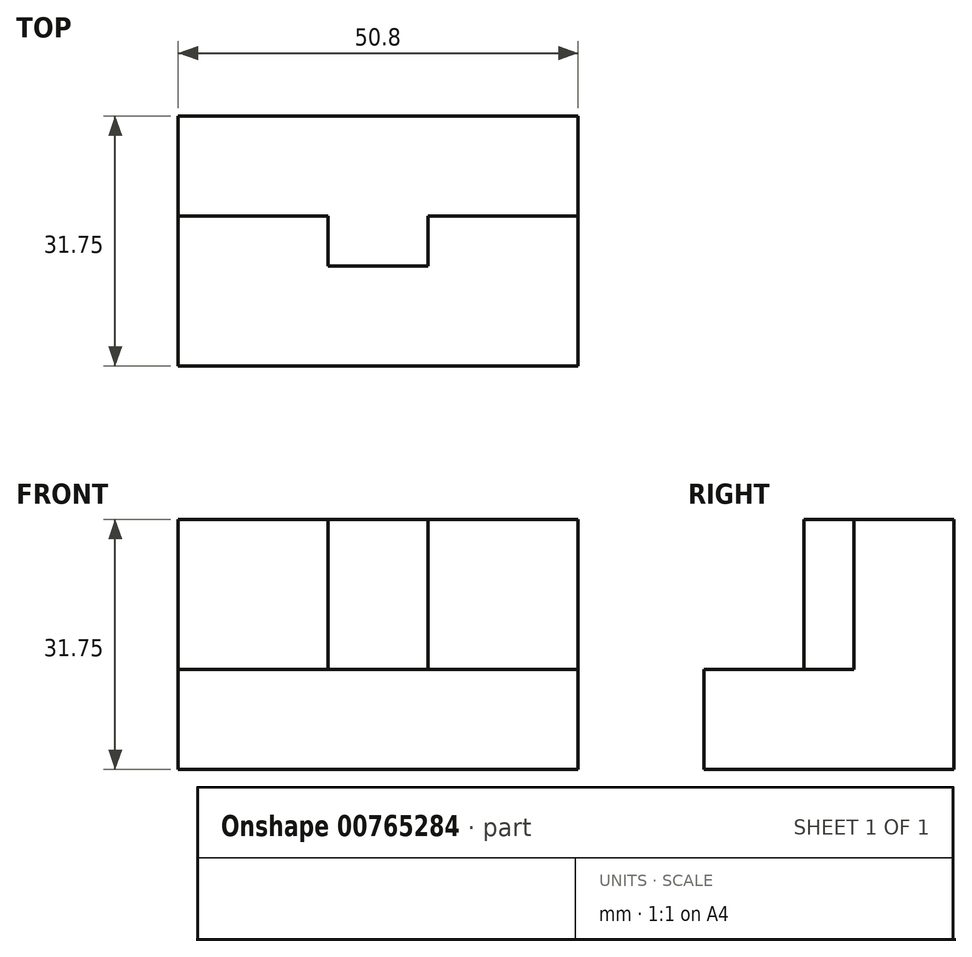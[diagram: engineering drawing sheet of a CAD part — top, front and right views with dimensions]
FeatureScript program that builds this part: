
annotation { "Feature Type Name" : "Feature", "Feature Type Description" : "" }
export const myFeature = defineFeature(function(context is Context, id is Id, definition is map)
    precondition{}
    {
        {
            var Q0;
            Q0=qCreatedBy(makeId("Front.planeOp"),FACE);
            var sketch = newSketch(context, id + "F0", { "sketchPlane" : qUnion([Q0])});
            skLineSegment(sketch, "E0", {"start": v(8.65, 2.43) * mm, "end": v(8.65, 34.18) * mm});
            skLineSegment(sketch, "E1", {"start": v(8.65, 2.43) * mm, "end": v(59.45, 2.43) * mm});
            skLineSegment(sketch, "E2", {"start": v(59.45, 2.43) * mm, "end": v(59.45, 34.18) * mm});
            skLineSegment(sketch, "E3", {"start": v(8.65, 34.18) * mm, "end": v(59.45, 34.18) * mm});
            skSolve(sketch);
        }
        {
            var Q0;
            Q0=makeQuery(id+"F0.imprint","IMPRINT",FACE,{"disambiguationData":[TD([[makeQuery(id+"F0.imprint","IMPRINT",EDGE,{"derivedFrom":sQuery(id+"F0.wireOp",EDGE,"E0")}),-1.0]])]});
            extrude(context, id + "F1", {"entities" : qUnion([Q0]), "depth" : 31.75 * mm, "offsetDistance" : 25.4 * mm});
        }
        {
            var Q0;
            Q0=makeQuery(id+"F1.opExtrude","CAP_FACE",FACE,{"disambiguationData":[OSD([sQuery(id+"F0.wireOp",EDGE,"E0"),sQuery(id+"F0.wireOp",EDGE,"E1"),sQuery(id+"F0.wireOp",EDGE,"E2"),sQuery(id+"F0.wireOp",EDGE,"E3")])],"isStart":false});
            var sketch = newSketch(context, id + "F2", { "sketchPlane" : qUnion([Q0])});
            skLineSegment(sketch, "E4", {"start": v(8.65, 2.43) * mm, "end": v(8.65, 15.13) * mm});
            skLineSegment(sketch, "E5", {"start": v(8.65, 15.13) * mm, "end": v(59.45, 15.13) * mm});
            skLineSegment(sketch, "E6", {"start": v(8.65, 34.18) * mm, "end": v(27.7, 34.18) * mm});
            skLineSegment(sketch, "E7", {"start": v(59.45, 34.18) * mm, "end": v(40.4, 34.18) * mm});
            skLineSegment(sketch, "E8", {"start": v(27.7, 34.18) * mm, "end": v(27.7, 15.13) * mm});
            skPoint(sketch, "E8.endSnap0", {"position": v(34.05, 15.13) * mm});
            skLineSegment(sketch, "E9", {"start": v(40.4, 34.18) * mm, "end": v(40.4, 15.13) * mm});
            skLineSegment(sketch, "E10", {"start": v(59.45, 15.13) * mm, "end": v(59.45, 34.18) * mm});
            skLineSegment(sketch, "E11", {"start": v(40.4, 34.18) * mm, "end": v(59.45, 34.18) * mm});
            skLineSegment(sketch, "E12", {"start": v(59.45, 34.18) * mm, "end": v(59.45, 15.13) * mm});
            skLineSegment(sketch, "E13", {"start": v(59.45, 15.13) * mm, "end": v(40.4, 15.13) * mm});
            skLineSegment(sketch, "E14", {"start": v(40.4, 15.13) * mm, "end": v(40.4, 34.18) * mm});
            skSolve(sketch);
        }
        {
            var Q0;
            {var subQ4=sQuery(id+"F2.wireOp",EDGE,"E6");Q0=makeQuery(id+"F2.imprint","IMPRINT",FACE,{"disambiguationData":[TD([[makeQuery(id+"F2.imprint","IMPRINT",EDGE,{"derivedFrom":subQ4}),-1.0]])]});}
            extrude(context, id + "F3", {"entities" : qUnion([Q0]), "operationType" : NewBodyOperationType.REMOVE, "oppositeDirection" : true, "depth" : 19.05 * mm, "offsetDistance" : 25.4 * mm});
        }
        {
            var Q0;
            Q0=makeQuery(id+"F1.opExtrude","CAP_FACE",FACE,{"disambiguationData":[OSD([sQuery(id+"F0.wireOp",EDGE,"E0"),sQuery(id+"F0.wireOp",EDGE,"E1"),sQuery(id+"F0.wireOp",EDGE,"E2"),sQuery(id+"F0.wireOp",EDGE,"E3")])],"isStart":false});
            var sketch = newSketch(context, id + "F4", { "sketchPlane" : qUnion([Q0])});
            skLineSegment(sketch, "E15", {"start": v(27.7, 34.18) * mm, "end": v(40.4, 34.18) * mm});
            skLineSegment(sketch, "E16", {"start": v(40.4, 34.18) * mm, "end": v(40.4, 15.13) * mm});
            skLineSegment(sketch, "E17", {"start": v(40.4, 15.13) * mm, "end": v(59.45, 15.13) * mm});
            skLineSegment(sketch, "E18", {"start": v(59.45, 15.13) * mm, "end": v(59.45, 34.18) * mm});
            skLineSegment(sketch, "E19", {"start": v(59.45, 34.18) * mm, "end": v(40.4, 34.18) * mm});
            skSolve(sketch);
        }
        {
            var Q0;
            Q0=makeQuery(id+"F4.imprint","IMPRINT",FACE,{"disambiguationData":[TD([[makeQuery(id+"F4.imprint","IMPRINT",EDGE,{"derivedFrom":sQuery(id+"F4.wireOp",EDGE,"E16")}),1.0]])]});
            extrude(context, id + "F5", {"entities" : qUnion([Q0]), "operationType" : NewBodyOperationType.REMOVE, "oppositeDirection" : true, "depth" : 19.05 * mm, "offsetDistance" : 25.4 * mm});
        }
        {
            var Q0;
            Q0=makeQuery(id+"F1.opExtrude","CAP_FACE",FACE,{"disambiguationData":[OSD([sQuery(id+"F0.wireOp",EDGE,"E0"),sQuery(id+"F0.wireOp",EDGE,"E1"),sQuery(id+"F0.wireOp",EDGE,"E2"),sQuery(id+"F0.wireOp",EDGE,"E3")])],"isStart":false});
            var sketch = newSketch(context, id + "F6", { "sketchPlane" : qUnion([Q0])});
            skLineSegment(sketch, "E20", {"start": v(27.7, 15.13) * mm, "end": v(40.4, 15.13) * mm});
            skLineSegment(sketch, "E21", {"start": v(40.4, 15.13) * mm, "end": v(40.4, 34.18) * mm});
            skLineSegment(sketch, "E22", {"start": v(40.4, 34.18) * mm, "end": v(27.7, 34.18) * mm});
            skLineSegment(sketch, "E23", {"start": v(157.9, -20) * mm, "end": v(164.99, -20) * mm});
            skSolve(sketch);
        }
        {
            var Q0;
            Q0=makeQuery(id+"F6.imprint","IMPRINT",FACE,{"disambiguationData":[TD([[makeQuery(id+"F6.imprint","IMPRINT",EDGE,{"derivedFrom":sQuery(id+"F6.wireOp",EDGE,"E20")}),1.0]])]});
            extrude(context, id + "F7", {"entities" : qUnion([Q0]), "operationType" : NewBodyOperationType.REMOVE, "oppositeDirection" : true, "depth" : 12.7 * mm, "offsetDistance" : 25.4 * mm});
        }
    });
